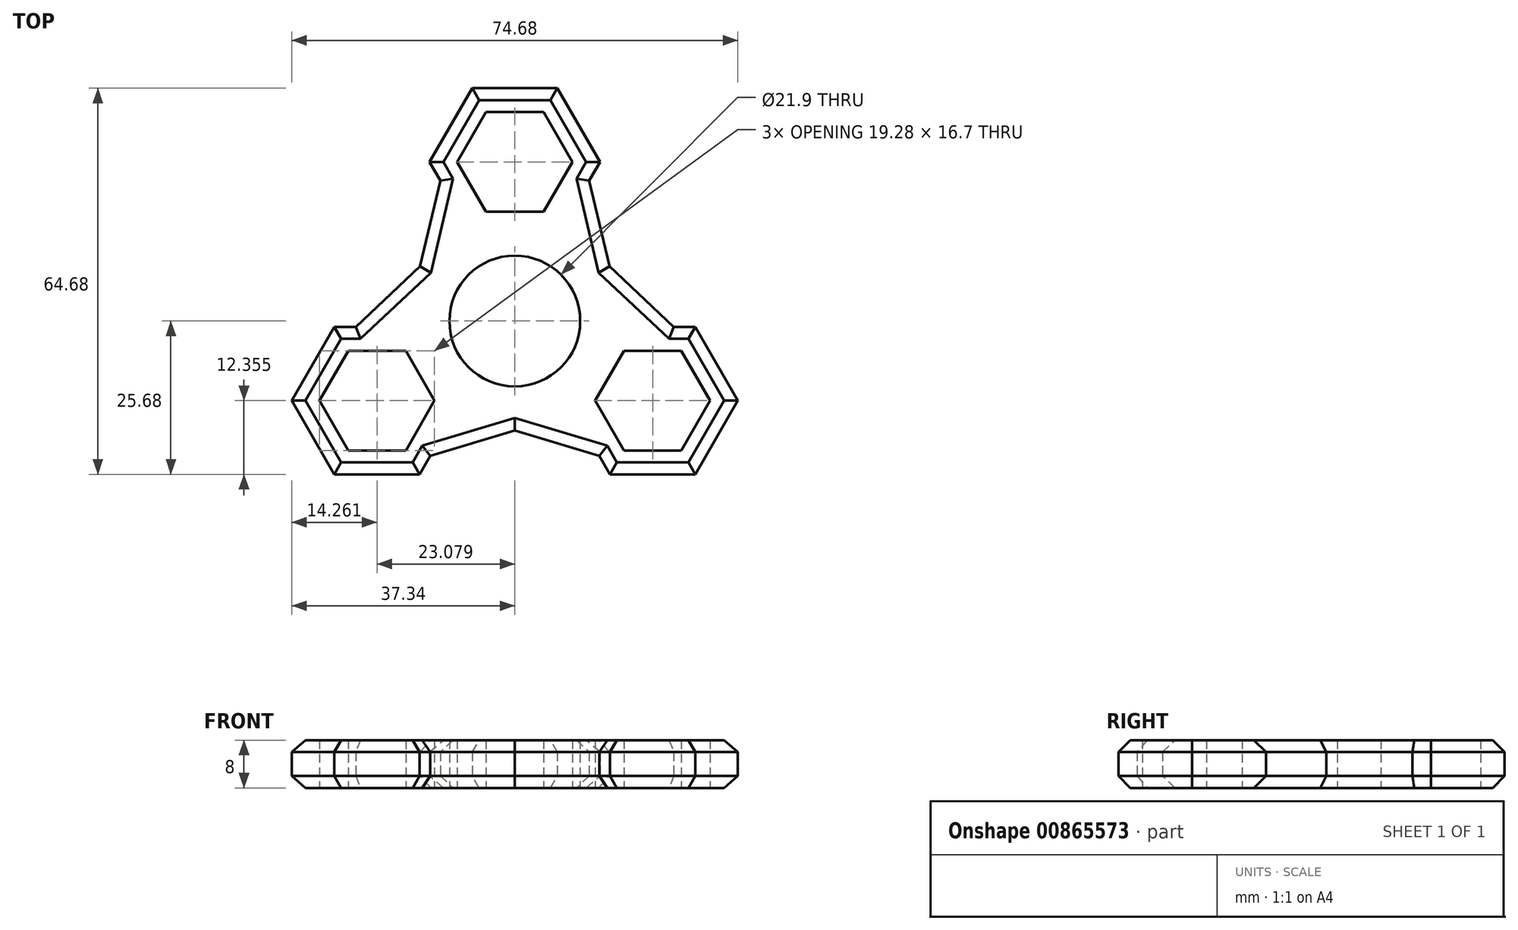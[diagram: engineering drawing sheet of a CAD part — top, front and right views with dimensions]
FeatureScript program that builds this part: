
annotation { "Feature Type Name" : "Feature", "Feature Type Description" : "" }
export const myFeature = defineFeature(function(context is Context, id is Id, definition is map)
    precondition{}
    {
        {
            var Q0;
            Q0=qCreatedBy(makeId("Top.planeOp"),FACE);
            var sketch = newSketch(context, id + "F0", { "sketchPlane" : qUnion([Q0])});
            skCircle(sketch, "E0", {"center": v(0, 0) * mm, "radius": 10.95 * mm});
            skCircle(sketch, "E1.cCircle", {"center": v(0, 26.65) * mm, "radius": 8.35 * mm, "construction": true});
            skLineSegment(sketch, "E1.0", {"start": v(4.82, 18.3) * mm, "end": v(-4.82, 18.3) * mm});
            skLineSegment(sketch, "E1.1", {"start": v(-4.82, 18.3) * mm, "end": v(-9.64, 26.65) * mm});
            skLineSegment(sketch, "E1.2", {"start": v(-9.64, 26.65) * mm, "end": v(-4.82, 35) * mm});
            skLineSegment(sketch, "E1.3", {"start": v(-4.82, 35) * mm, "end": v(4.82, 35) * mm});
            skLineSegment(sketch, "E1.4", {"start": v(4.82, 35) * mm, "end": v(9.64, 26.65) * mm});
            skLineSegment(sketch, "E1.5", {"start": v(9.64, 26.65) * mm, "end": v(4.82, 18.3) * mm});
            skPoint(sketch, "E1.0.midPoint", {"position": v(0, 18.3) * mm});
            skCircle(sketch, "E2", {"center": v(0, 0) * mm, "radius": 26.65 * mm, "construction": true});
            skLineSegment(sketch, "E3", {"start": v(-27.4, 15.83) * mm, "end": v(0, 0) * mm, "construction": true});
            skLineSegment(sketch, "E4", {"start": v(27.4, 15.82) * mm, "end": v(0, 0) * mm, "construction": true});
            skLineSegment(sketch, "E5", {"start": v(0, 0) * mm, "end": v(0, -31.65) * mm, "construction": true});
            skLineSegment(sketch, "E6.0", {"start": v(-14.26, 26.65) * mm, "end": v(-7.13, 39) * mm});
            skLineSegment(sketch, "E6.1", {"start": v(7.13, 39) * mm, "end": v(14.26, 26.65) * mm});
            skLineSegment(sketch, "E6.2", {"start": v(14.26, 26.65) * mm, "end": v(12.47, 23.55) * mm});
            skLineSegment(sketch, "E6.3", {"start": v(-7.13, 39) * mm, "end": v(7.13, 39) * mm});
            skLineSegment(sketch, "E6.5", {"start": v(-12.47, 23.55) * mm, "end": v(-14.26, 26.65) * mm});
            skLineSegment(sketch, "E7.1.0", {"start": v(-30.2, -25.67) * mm, "end": v(-37.34, -13.32) * mm});
            skLineSegment(sketch, "E7.1.1", {"start": v(-37.34, -13.33) * mm, "end": v(-30.2, -0.97) * mm});
            skPoint(sketch, "E7.1.2", {"position": v(-15.85, -9.15) * mm});
            skCircle(sketch, "E7.1.3", {"center": v(-23.08, -13.32) * mm, "radius": 8.35 * mm, "construction": true});
            skLineSegment(sketch, "E7.1.4", {"start": v(-14.16, -22.58) * mm, "end": v(-15.95, -25.67) * mm});
            skLineSegment(sketch, "E7.1.5", {"start": v(-15.95, -25.67) * mm, "end": v(-30.2, -25.67) * mm});
            skLineSegment(sketch, "E7.1.6", {"start": v(-30.2, -0.98) * mm, "end": v(-26.63, -0.98) * mm});
            skLineSegment(sketch, "E7.1.8", {"start": v(-13.44, -13.32) * mm, "end": v(-18.26, -21.68) * mm});
            skLineSegment(sketch, "E7.1.9", {"start": v(-18.26, -21.68) * mm, "end": v(-27.9, -21.67) * mm});
            skLineSegment(sketch, "E7.1.10", {"start": v(-18.26, -4.98) * mm, "end": v(-13.44, -13.32) * mm});
            skLineSegment(sketch, "E7.1.11", {"start": v(-32.72, -13.32) * mm, "end": v(-27.9, -4.97) * mm});
            skLineSegment(sketch, "E7.1.12", {"start": v(-27.9, -4.97) * mm, "end": v(-18.26, -4.97) * mm});
            skLineSegment(sketch, "E7.1.13", {"start": v(-27.9, -21.67) * mm, "end": v(-32.72, -13.32) * mm});
            skLineSegment(sketch, "E7.2.0", {"start": v(37.34, -13.33) * mm, "end": v(30.2, -25.68) * mm});
            skLineSegment(sketch, "E7.2.1", {"start": v(30.2, -25.68) * mm, "end": v(15.95, -25.68) * mm});
            skPoint(sketch, "E7.2.2", {"position": v(15.85, -9.15) * mm});
            skCircle(sketch, "E7.2.3", {"center": v(23.08, -13.33) * mm, "radius": 8.35 * mm, "construction": true});
            skLineSegment(sketch, "E7.2.4", {"start": v(26.63, -0.98) * mm, "end": v(30.2, -0.98) * mm});
            skLineSegment(sketch, "E7.2.5", {"start": v(30.2, -0.98) * mm, "end": v(37.34, -13.33) * mm});
            skLineSegment(sketch, "E7.2.6", {"start": v(15.95, -25.68) * mm, "end": v(14.16, -22.58) * mm});
            skLineSegment(sketch, "E7.2.8", {"start": v(18.26, -4.98) * mm, "end": v(27.9, -4.98) * mm});
            skLineSegment(sketch, "E7.2.9", {"start": v(27.9, -4.98) * mm, "end": v(32.72, -13.33) * mm});
            skLineSegment(sketch, "E7.2.10", {"start": v(13.44, -13.32) * mm, "end": v(18.26, -4.98) * mm});
            skLineSegment(sketch, "E7.2.11", {"start": v(27.9, -21.68) * mm, "end": v(18.26, -21.68) * mm});
            skLineSegment(sketch, "E7.2.12", {"start": v(18.26, -21.68) * mm, "end": v(13.44, -13.32) * mm});
            skLineSegment(sketch, "E7.2.13", {"start": v(32.72, -13.33) * mm, "end": v(27.9, -21.68) * mm});
            skCircle(sketch, "E8", {"center": v(0, 0) * mm, "radius": 18.3 * mm, "construction": true});
            skLineSegment(sketch, "E9", {"start": v(-12.47, 23.55) * mm, "end": v(-15.85, 9.15) * mm});
            skLineSegment(sketch, "E10", {"start": v(-15.85, 9.15) * mm, "end": v(-26.63, -0.98) * mm});
            skLineSegment(sketch, "E11", {"start": v(-14.16, -22.58) * mm, "end": v(0, -18.3) * mm});
            skLineSegment(sketch, "E12", {"start": v(0, -18.3) * mm, "end": v(14.16, -22.58) * mm});
            skLineSegment(sketch, "E13", {"start": v(26.63, -0.98) * mm, "end": v(15.85, 9.15) * mm});
            skLineSegment(sketch, "E14", {"start": v(15.85, 9.15) * mm, "end": v(12.47, 23.55) * mm});
            skSolve(sketch);
        }
        {
            var Q0;
            Q0=qSketchRegion(id+"F0",true);
            extrude(context, id + "F1", {"entities" : qUnion([Q0]), "endBound" : BoundingType.SYMMETRIC, "depth" : 8 * mm, "offsetDistance" : 25 * mm});
        }
        {
            var Q0;
            Q0=makeQuery(id+"F1.opExtrude","CAP_EDGE",EDGE,{"disambiguationData":[OSD([sQuery(id+"F0.wireOp",EDGE,"E6.1")])],"isStart":false});
            var Q1;
            Q1=makeQuery(id+"F1.opExtrude","CAP_EDGE",EDGE,{"disambiguationData":[OSD([sQuery(id+"F0.wireOp",EDGE,"E6.3")])],"isStart":false});
            var Q2;
            Q2=makeQuery(id+"F1.opExtrude","CAP_EDGE",EDGE,{"disambiguationData":[OSD([sQuery(id+"F0.wireOp",EDGE,"E6.0")])],"isStart":false});
            var Q3;
            Q3=makeQuery(id+"F1.opExtrude","CAP_EDGE",EDGE,{"disambiguationData":[OSD([sQuery(id+"F0.wireOp",EDGE,"E6.5")])],"isStart":false});
            var Q4;
            Q4=makeQuery(id+"F1.opExtrude","CAP_EDGE",EDGE,{"disambiguationData":[OSD([sQuery(id+"F0.wireOp",EDGE,"E6.2")])],"isStart":false});
            var Q5;
            Q5=makeQuery(id+"F1.opExtrude","CAP_EDGE",EDGE,{"disambiguationData":[OSD([sQuery(id+"F0.wireOp",EDGE,"E14")])],"isStart":false});
            var Q6;
            Q6=makeQuery(id+"F1.opExtrude","CAP_EDGE",EDGE,{"disambiguationData":[OSD([sQuery(id+"F0.wireOp",EDGE,"E13")])],"isStart":false});
            var Q7;
            Q7=makeQuery(id+"F1.opExtrude","CAP_EDGE",EDGE,{"disambiguationData":[OSD([sQuery(id+"F0.wireOp",EDGE,"E7.2.4")])],"isStart":false});
            var Q8;
            Q8=makeQuery(id+"F1.opExtrude","CAP_EDGE",EDGE,{"disambiguationData":[OSD([sQuery(id+"F0.wireOp",EDGE,"E7.2.5")])],"isStart":false});
            var Q9;
            Q9=makeQuery(id+"F1.opExtrude","CAP_EDGE",EDGE,{"disambiguationData":[OSD([sQuery(id+"F0.wireOp",EDGE,"E7.2.0")])],"isStart":false});
            var Q10;
            Q10=makeQuery(id+"F1.opExtrude","CAP_EDGE",EDGE,{"disambiguationData":[OSD([sQuery(id+"F0.wireOp",EDGE,"E7.2.1")])],"isStart":false});
            var Q11;
            Q11=makeQuery(id+"F1.opExtrude","CAP_EDGE",EDGE,{"disambiguationData":[OSD([sQuery(id+"F0.wireOp",EDGE,"E12")])],"isStart":false});
            var Q12;
            Q12=makeQuery(id+"F1.opExtrude","CAP_EDGE",EDGE,{"disambiguationData":[OSD([sQuery(id+"F0.wireOp",EDGE,"E11")])],"isStart":false});
            var Q13;
            Q13=makeQuery(id+"F1.opExtrude","CAP_EDGE",EDGE,{"disambiguationData":[OSD([sQuery(id+"F0.wireOp",EDGE,"E7.1.4")])],"isStart":false});
            var Q14;
            Q14=makeQuery(id+"F1.opExtrude","CAP_EDGE",EDGE,{"disambiguationData":[OSD([sQuery(id+"F0.wireOp",EDGE,"E7.2.6")])],"isStart":false});
            var Q15;
            Q15=makeQuery(id+"F1.opExtrude","CAP_EDGE",EDGE,{"disambiguationData":[OSD([sQuery(id+"F0.wireOp",EDGE,"E7.1.5")])],"isStart":false});
            var Q16;
            Q16=makeQuery(id+"F1.opExtrude","CAP_EDGE",EDGE,{"disambiguationData":[OSD([sQuery(id+"F0.wireOp",EDGE,"E7.1.0")])],"isStart":false});
            var Q17;
            Q17=makeQuery(id+"F1.opExtrude","CAP_EDGE",EDGE,{"disambiguationData":[OSD([sQuery(id+"F0.wireOp",EDGE,"E7.1.1")])],"isStart":false});
            var Q18;
            Q18=makeQuery(id+"F1.opExtrude","CAP_EDGE",EDGE,{"disambiguationData":[OSD([sQuery(id+"F0.wireOp",EDGE,"E10")])],"isStart":false});
            var Q19;
            Q19=makeQuery(id+"F1.opExtrude","CAP_EDGE",EDGE,{"disambiguationData":[OSD([sQuery(id+"F0.wireOp",EDGE,"E9")])],"isStart":false});
            var Q20;
            Q20=makeQuery(id+"F1.opExtrude","CAP_EDGE",EDGE,{"disambiguationData":[OSD([sQuery(id+"F0.wireOp",EDGE,"E7.1.6")])],"isStart":false});
            var Q21;
            Q21=makeQuery(id+"F1.opExtrude","CAP_EDGE",EDGE,{"disambiguationData":[OSD([sQuery(id+"F0.wireOp",EDGE,"E10")])],"isStart":true});
            var Q22;
            Q22=makeQuery(id+"F1.opExtrude","CAP_EDGE",EDGE,{"disambiguationData":[OSD([sQuery(id+"F0.wireOp",EDGE,"E9")])],"isStart":true});
            var Q23;
            Q23=makeQuery(id+"F1.opExtrude","CAP_EDGE",EDGE,{"disambiguationData":[OSD([sQuery(id+"F0.wireOp",EDGE,"E6.5")])],"isStart":true});
            var Q24;
            Q24=makeQuery(id+"F1.opExtrude","CAP_EDGE",EDGE,{"disambiguationData":[OSD([sQuery(id+"F0.wireOp",EDGE,"E6.0")])],"isStart":true});
            var Q25;
            Q25=makeQuery(id+"F1.opExtrude","CAP_EDGE",EDGE,{"disambiguationData":[OSD([sQuery(id+"F0.wireOp",EDGE,"E6.3")])],"isStart":true});
            var Q26;
            Q26=makeQuery(id+"F1.opExtrude","CAP_EDGE",EDGE,{"disambiguationData":[OSD([sQuery(id+"F0.wireOp",EDGE,"E6.1")])],"isStart":true});
            var Q27;
            Q27=makeQuery(id+"F1.opExtrude","CAP_EDGE",EDGE,{"disambiguationData":[OSD([sQuery(id+"F0.wireOp",EDGE,"E6.2")])],"isStart":true});
            var Q28;
            Q28=makeQuery(id+"F1.opExtrude","CAP_EDGE",EDGE,{"disambiguationData":[OSD([sQuery(id+"F0.wireOp",EDGE,"E14")])],"isStart":true});
            var Q29;
            Q29=makeQuery(id+"F1.opExtrude","CAP_EDGE",EDGE,{"disambiguationData":[OSD([sQuery(id+"F0.wireOp",EDGE,"E13")])],"isStart":true});
            var Q30;
            Q30=makeQuery(id+"F1.opExtrude","CAP_EDGE",EDGE,{"disambiguationData":[OSD([sQuery(id+"F0.wireOp",EDGE,"E7.2.4")])],"isStart":true});
            var Q31;
            Q31=makeQuery(id+"F1.opExtrude","CAP_EDGE",EDGE,{"disambiguationData":[OSD([sQuery(id+"F0.wireOp",EDGE,"E7.2.5")])],"isStart":true});
            var Q32;
            Q32=makeQuery(id+"F1.opExtrude","CAP_EDGE",EDGE,{"disambiguationData":[OSD([sQuery(id+"F0.wireOp",EDGE,"E7.2.0")])],"isStart":true});
            var Q33;
            Q33=makeQuery(id+"F1.opExtrude","CAP_EDGE",EDGE,{"disambiguationData":[OSD([sQuery(id+"F0.wireOp",EDGE,"E7.2.1")])],"isStart":true});
            var Q34;
            Q34=makeQuery(id+"F1.opExtrude","CAP_EDGE",EDGE,{"disambiguationData":[OSD([sQuery(id+"F0.wireOp",EDGE,"E7.2.6")])],"isStart":true});
            var Q35;
            Q35=makeQuery(id+"F1.opExtrude","CAP_EDGE",EDGE,{"disambiguationData":[OSD([sQuery(id+"F0.wireOp",EDGE,"E12")])],"isStart":true});
            var Q36;
            Q36=makeQuery(id+"F1.opExtrude","CAP_EDGE",EDGE,{"disambiguationData":[OSD([sQuery(id+"F0.wireOp",EDGE,"E11")])],"isStart":true});
            var Q37;
            Q37=makeQuery(id+"F1.opExtrude","CAP_EDGE",EDGE,{"disambiguationData":[OSD([sQuery(id+"F0.wireOp",EDGE,"E7.1.4")])],"isStart":true});
            var Q38;
            Q38=makeQuery(id+"F1.opExtrude","CAP_EDGE",EDGE,{"disambiguationData":[OSD([sQuery(id+"F0.wireOp",EDGE,"E7.1.5")])],"isStart":true});
            var Q39;
            Q39=makeQuery(id+"F1.opExtrude","CAP_EDGE",EDGE,{"disambiguationData":[OSD([sQuery(id+"F0.wireOp",EDGE,"E7.1.0")])],"isStart":true});
            var Q40;
            Q40=makeQuery(id+"F1.opExtrude","CAP_EDGE",EDGE,{"disambiguationData":[OSD([sQuery(id+"F0.wireOp",EDGE,"E7.1.1")])],"isStart":true});
            var Q41;
            Q41=makeQuery(id+"F1.opExtrude","CAP_EDGE",EDGE,{"disambiguationData":[OSD([sQuery(id+"F0.wireOp",EDGE,"E7.1.6")])],"isStart":true});
            chamfer(context, id + "F2", {"entities" : qUnion([Q0, Q1, Q2, Q3, Q4, Q5, Q6, Q7, Q8, Q9, Q10, Q11, Q12, Q13, Q14, Q15, Q16, Q17, Q18, Q19, Q20, Q21, Q22, Q23, Q24, Q25, Q26, Q27, Q28, Q29, Q30, Q31, Q32, Q33, Q34, Q35, Q36, Q37, Q38, Q39, Q40, Q41]), "width" : 2 * mm, "tangentPropagation" : true});
        }
    });
